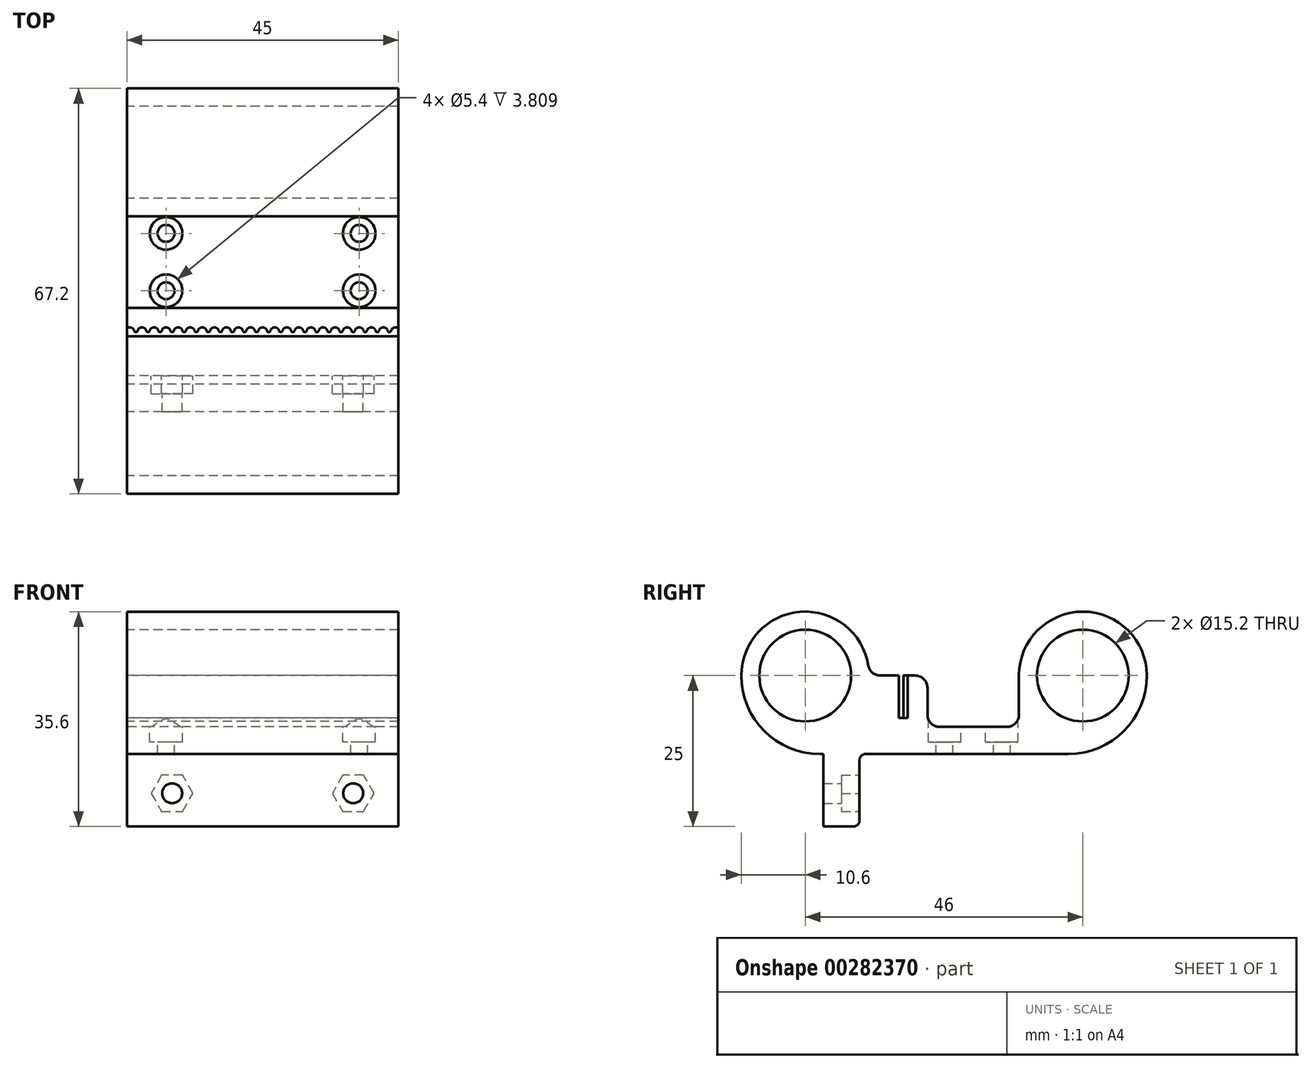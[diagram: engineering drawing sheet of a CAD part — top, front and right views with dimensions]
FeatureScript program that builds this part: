
annotation { "Feature Type Name" : "Feature", "Feature Type Description" : "" }
export const myFeature = defineFeature(function(context is Context, id is Id, definition is map)
    precondition{}
    {
        {
            var Q0;
            Q0=qCreatedBy(makeId("Right.planeOp"),FACE);
            var sketch = newSketch(context, id + "F0", { "sketchPlane" : qUnion([Q0])});
            skCircle(sketch, "E0", {"center": v(0, 0) * mm, "radius": 7.6 * mm});
            skLineSegment(sketch, "E1", {"start": v(0, 0) * mm, "end": v(46, 0) * mm, "construction": true});
            skCircle(sketch, "E2", {"center": v(46, 0) * mm, "radius": 7.6 * mm});
            skArc(sketch, "E3", {"start": v(10.47, 1.68) * mm, "mid": v(-0.84, 10.57) * mm, "end": v(-10.6, 0) * mm});
            skArc(sketch, "E4", {"start": v(56.6, 0) * mm, "mid": v(46, 10.6) * mm, "end": v(35.4, 0) * mm});
            skLineSegment(sketch, "E5", {"start": v(15.5, -7) * mm, "end": v(16.25, -7) * mm});
            skPoint(sketch, "E6.orphan", {"position": v(46, -7.6) * mm});
            skPoint(sketch, "E7.orphan", {"position": v(0, -7.6) * mm});
            skLineSegment(sketch, "E8", {"start": v(12.44, 0) * mm, "end": v(15.5, 0) * mm});
            skLineSegment(sketch, "E9", {"start": v(15.5, 0) * mm, "end": v(15.5, -7) * mm});
            skLineSegment(sketch, "E10", {"start": v(16.25, -7) * mm, "end": v(16.25, 0) * mm});
            skLineSegment(sketch, "E11", {"start": v(16.25, 0) * mm, "end": v(18.25, 0) * mm});
            skLineSegment(sketch, "E12", {"start": v(20.25, -2) * mm, "end": v(20.25, -6.5) * mm});
            skLineSegment(sketch, "E13.trimOffspring", {"start": v(22.25, -8.5) * mm, "end": v(33.4, -8.5) * mm});
            skLineSegment(sketch, "E14", {"start": v(35.4, 0) * mm, "end": v(35.4, -6.5) * mm});
            skPoint(sketch, "E15.visualSharp", {"position": v(20.25, 0) * mm});
            skArc(sketch, "E15.filletArc", {"start": v(20.25, -2) * mm, "mid": v(19.66, -0.59) * mm, "end": v(18.25, 0) * mm});
            skPoint(sketch, "E16.visualSharp", {"position": v(20.25, -8.5) * mm});
            skArc(sketch, "E16.filletArc", {"start": v(20.25, -6.5) * mm, "mid": v(20.84, -7.91) * mm, "end": v(22.25, -8.5) * mm});
            skPoint(sketch, "E17.visualSharp", {"position": v(35.4, -8.5) * mm});
            skArc(sketch, "E17.filletArc", {"start": v(33.4, -8.5) * mm, "mid": v(34.81, -7.91) * mm, "end": v(35.4, -6.5) * mm});
            skLineSegment(sketch, "E18", {"start": v(3, -25) * mm, "end": v(8, -25) * mm});
            skLineSegment(sketch, "E19", {"start": v(9, -24) * mm, "end": v(9, -14) * mm});
            skPoint(sketch, "E20.visualSharp", {"position": v(9, -13) * mm});
            skArc(sketch, "E20.filletArc", {"start": v(10, -13) * mm, "mid": v(9.3, -13.3) * mm, "end": v(9, -14) * mm});
            skPoint(sketch, "E21.visualSharp", {"position": v(9, -25) * mm});
            skArc(sketch, "E21.filletArc", {"start": v(8, -25) * mm, "mid": v(8.7, -24.7) * mm, "end": v(9, -24) * mm});
            skLineSegment(sketch, "E22", {"start": v(53.6, 0) * mm, "end": v(56.6, 0) * mm, "construction": true});
            skArc(sketch, "E23", {"start": v(43.6, -13) * mm, "mid": v(52.8, -9.2) * mm, "end": v(56.6, 0) * mm});
            skPoint(sketch, "E24.visualSharp", {"position": v(10.6, 0) * mm});
            skArc(sketch, "E24.filletArc", {"start": v(10.47, 1.68) * mm, "mid": v(11.14, 0.48) * mm, "end": v(12.44, 0) * mm});
            skLineSegment(sketch, "E25", {"start": v(9, -13) * mm, "end": v(3, -13) * mm, "construction": true});
            skLineSegment(sketch, "E26", {"start": v(10, -13) * mm, "end": v(43.6, -13) * mm});
            skLineSegment(sketch, "E27", {"start": v(3, -13) * mm, "end": v(3, -25) * mm});
            skLineSegment(sketch, "E28", {"start": v(2.4, -13) * mm, "end": v(3, -13) * mm});
            skLineSegment(sketch, "E29", {"start": v(23, 0) * mm, "end": v(23, 8.24) * mm, "construction": true});
            skArc(sketch, "E30.MirrorCS", {"start": v(2.4, -13) * mm, "mid": v(-6.8, -9.2) * mm, "end": v(-10.6, 0) * mm});
            skSolve(sketch);
        }
        {
            var Q0;
            Q0 = qSketchRegion(id + "F0", true);
            extrude(context, id + "F1", {"entities" : qUnion([Q0]), "depth" : 45 * mm});
        }
        {
            var Q0;
            Q0=makeQuery(id+"F1.opExtrude","SWEPT_FACE",FACE,{"disambiguationData":[OSD([sQuery(id+"F0.wireOp",EDGE,"E19")])]});
            var sketch = newSketch(context, id + "F2", { "sketchPlane" : qUnion([Q0])});
            skLineSegment(sketch, "E31", {"start": v(-45, -19.5) * mm, "end": v(0, -19.5) * mm, "construction": true});
            skLineSegment(sketch, "E32", {"start": v(-22.5, -19.5) * mm, "end": v(-22.5, -24) * mm, "construction": true});
            skCircle(sketch, "E33.cCircle", {"center": v(-37.5, -19.5) * mm, "radius": 3 * mm, "construction": true});
            skLineSegment(sketch, "E33.0", {"start": v(-35.77, -22.5) * mm, "end": v(-39.23, -22.5) * mm});
            skLineSegment(sketch, "E33.1", {"start": v(-39.23, -22.5) * mm, "end": v(-40.96, -19.5) * mm});
            skLineSegment(sketch, "E33.2", {"start": v(-40.96, -19.5) * mm, "end": v(-39.23, -16.5) * mm});
            skLineSegment(sketch, "E33.3", {"start": v(-39.23, -16.5) * mm, "end": v(-35.77, -16.5) * mm});
            skLineSegment(sketch, "E33.4", {"start": v(-35.77, -16.5) * mm, "end": v(-34.04, -19.5) * mm});
            skLineSegment(sketch, "E33.5", {"start": v(-34.04, -19.5) * mm, "end": v(-35.77, -22.5) * mm});
            skPoint(sketch, "E33.0.midPoint", {"position": v(-37.5, -22.5) * mm});
            skCircle(sketch, "E34.cCircle", {"center": v(-7.5, -19.5) * mm, "radius": 3 * mm, "construction": true});
            skLineSegment(sketch, "E34.0", {"start": v(-5.77, -22.5) * mm, "end": v(-9.23, -22.5) * mm});
            skLineSegment(sketch, "E34.1", {"start": v(-9.23, -22.5) * mm, "end": v(-10.96, -19.5) * mm});
            skLineSegment(sketch, "E34.2", {"start": v(-10.96, -19.5) * mm, "end": v(-9.23, -16.5) * mm});
            skLineSegment(sketch, "E34.3", {"start": v(-9.23, -16.5) * mm, "end": v(-5.77, -16.5) * mm});
            skLineSegment(sketch, "E34.4", {"start": v(-5.77, -16.5) * mm, "end": v(-4.04, -19.5) * mm});
            skLineSegment(sketch, "E34.5", {"start": v(-4.04, -19.5) * mm, "end": v(-5.77, -22.5) * mm});
            skPoint(sketch, "E34.0.midPoint", {"position": v(-7.5, -22.5) * mm});
            skSolve(sketch);
        }
        {
            var Q0;
            Q0 = qSketchRegion(id + "F2", true);
            extrude(context, id + "F3", {"entities" : qUnion([Q0]), "operationType" : NewBodyOperationType.REMOVE, "oppositeDirection" : true, "depth" : 3 * mm});
        }
        {
            var Q0;
            Q0=sQuery(id+"F2.wireOp",VERTEX,"E33.cCircle.center");
            var Q1;
            Q1=sQuery(id+"F2.wireOp",VERTEX,"E34.cCircle.center");
            var Q2;
            Q2=makeQuery(id+"F1.opExtrude","SWEPT_BODY",BODY,{"disambiguationData":[OSD([sQuery(id+"F0.wireOp",EDGE,"E0"),sQuery(id+"F0.wireOp",EDGE,"E2"),sQuery(id+"F0.wireOp",EDGE,"E3"),sQuery(id+"F0.wireOp",EDGE,"E4"),sQuery(id+"F0.wireOp",EDGE,"j08GQjmV-9Uym-nQLd-N5JK-njCeGAc3z8Nu"),sQuery(id+"F0.wireOp",EDGE,"E5"),sQuery(id+"F0.wireOp",EDGE,"E8"),sQuery(id+"F0.wireOp",EDGE,"E9"),sQuery(id+"F0.wireOp",EDGE,"E10"),sQuery(id+"F0.wireOp",EDGE,"E11"),sQuery(id+"F0.wireOp",EDGE,"E12"),sQuery(id+"F0.wireOp",EDGE,"E13.trimOffspring"),sQuery(id+"F0.wireOp",EDGE,"E14"),sQuery(id+"F0.wireOp",EDGE,"E15.filletArc"),sQuery(id+"F0.wireOp",EDGE,"E16.filletArc"),sQuery(id+"F0.wireOp",EDGE,"E17.filletArc"),sQuery(id+"F0.wireOp",EDGE,"HgORvXto-rNN1-qf5N-DkuC-96ioj9euDlec"),sQuery(id+"F0.wireOp",EDGE,"E18"),sQuery(id+"F0.wireOp",EDGE,"E19"),sQuery(id+"F0.wireOp",EDGE,"e149524c-0aa9-48c4-a7ad-8e2e2100d5f0.filletArc"),sQuery(id+"F0.wireOp",EDGE,"65fca797-e460-4261-b8cc-2deb6b025714.filletArc")])]});
            hole(context, id + "F4", {"style" : HoleStyle.SIMPLE, "endStyle" : HoleEndStyle.THROUGH, "standardTappedOrClearance" : lookupTablePath({ "standard" : "ISO", "fit" : "Normal", "size" : "M3", "type" : "Clearance" }), "standardBlindInLast" : lookupTablePath({ "fit" : "Standard", "standard" : "ISO", "size" : "M3", "type" : "Clearance" }), "holeDiameter" : 3.3 * mm, "tappedDepth" : 3 * mm, "tapClearance" : 3, "startFromSketch" : true, "locations" : qUnion([Q0, Q1]), "scope" : qUnion([Q2])});
        }
        {
            var Q0;
            Q0=makeQuery(id+"F1.opExtrude","SWEPT_FACE",FACE,{"disambiguationData":[OSD([sQuery(id+"F0.wireOp",EDGE,"E13.trimOffspring")])]});
            var sketch = newSketch(context, id + "F5", { "sketchPlane" : qUnion([Q0])});
            skLineSegment(sketch, "E35", {"start": v(0, 27.82) * mm, "end": v(45, 27.82) * mm, "construction": true});
            skLineSegment(sketch, "E36", {"start": v(6.5, 32.57) * mm, "end": v(6.5, 23.07) * mm, "construction": true});
            skLineSegment(sketch, "E37", {"start": v(38.5, 32.58) * mm, "end": v(38.5, 23.07) * mm, "construction": true});
            skCircle(sketch, "E38", {"center": v(6.5, 32.57) * mm, "radius": 1.4 * mm});
            skCircle(sketch, "E39", {"center": v(6.5, 23.07) * mm, "radius": 1.4 * mm});
            skCircle(sketch, "E40", {"center": v(38.5, 23.07) * mm, "radius": 1.4 * mm});
            skCircle(sketch, "E41", {"center": v(38.5, 32.58) * mm, "radius": 1.4 * mm});
            skSolve(sketch);
        }
        {
            var Q0;
            Q0 = qSketchRegion(id + "F5", true);
            extrude(context, id + "F6", {"entities" : qUnion([Q0]), "operationType" : NewBodyOperationType.REMOVE, "endBound" : BoundingType.SYMMETRIC, "oppositeDirection" : true, "depth" : 25 * mm});
        }
        {
            var Q0;
            Q0=makeQuery(id+"F1.opExtrude","SWEPT_FACE",FACE,{"disambiguationData":[OSD([sQuery(id+"F0.wireOp",EDGE,"E13.trimOffspring")])]});
            var sketch = newSketch(context, id + "F7", { "sketchPlane" : qUnion([Q0])});
            skCircle(sketch, "E42", {"center": v(6.5, 32.57) * mm, "radius": 2.7 * mm});
            skCircle(sketch, "E43", {"center": v(38.5, 32.58) * mm, "radius": 2.7 * mm});
            skCircle(sketch, "E44", {"center": v(38.5, 23.07) * mm, "radius": 2.7 * mm});
            skCircle(sketch, "E45", {"center": v(6.5, 23.07) * mm, "radius": 2.7 * mm});
            skSolve(sketch);
        }
        {
            var Q0;
            Q0 = qSketchRegion(id + "F7", true);
            extrude(context, id + "F8", {"entities" : qUnion([Q0]), "operationType" : NewBodyOperationType.REMOVE, "oppositeDirection" : true, "depth" : 2.5 * mm});
        }
        {
            var Q0;
            Q0=makeQuery(id+"F1.opExtrude","SWEPT_FACE",FACE,{"disambiguationData":[OSD([sQuery(id+"F0.wireOp",EDGE,"E13.trimOffspring")])]});
            var sketch = newSketch(context, id + "F9", { "sketchPlane" : qUnion([Q0])});
            skCircle(sketch, "E46", {"center": v(6.5, 32.57) * mm, "radius": 2.7 * mm});
            skCircle(sketch, "E47", {"center": v(38.5, 32.58) * mm, "radius": 2.7 * mm});
            skCircle(sketch, "E48", {"center": v(38.5, 23.07) * mm, "radius": 2.7 * mm});
            skCircle(sketch, "E49", {"center": v(6.5, 23.07) * mm, "radius": 2.7 * mm});
            skSolve(sketch);
        }
        {
            var Q0;
            Q0 = qSketchRegion(id + "F9", true);
            extrude(context, id + "F10", {"entities" : qUnion([Q0]), "operationType" : NewBodyOperationType.REMOVE, "depth" : 25 * mm});
        }
        {
            var Q0;
            Q0=makeQuery(id+"F1.opExtrude","SWEPT_FACE",FACE,{"disambiguationData":[OSD([sQuery(id+"F0.wireOp",EDGE,"E11")])]});
            var sketch = newSketch(context, id + "F11", { "sketchPlane" : qUnion([Q0])});
            skLineSegment(sketch, "E50", {"start": v(45, 17) * mm, "end": v(0, 17) * mm, "construction": true});
            skPoint(sketch, "E50.endSnap0", {"position": v(0, 17.25) * mm});
            skLineSegment(sketch, "E51", {"start": v(22.5, 17) * mm, "end": v(22.5, 16.25) * mm, "construction": true});
            skLineSegment(sketch, "E52", {"start": v(20.5, 17) * mm, "end": v(20.5, 16.25) * mm, "construction": true});
            skLineSegment(sketch, "E53", {"start": v(24.5, 17) * mm, "end": v(24.5, 16.25) * mm, "construction": true});
            skArc(sketch, "E54", {"start": v(23.24, 16.38) * mm, "mid": v(22.5, 17) * mm, "end": v(21.76, 16.38) * mm});
            skLineSegment(sketch, "E55", {"start": v(21.5, 16.25) * mm, "end": v(21.61, 16.25) * mm});
            skLineSegment(sketch, "E56", {"start": v(21.5, 17) * mm, "end": v(21.5, 16.25) * mm, "construction": true});
            skLineSegment(sketch, "E57", {"start": v(23.5, 17) * mm, "end": v(23.5, 16.25) * mm, "construction": true});
            skLineSegment(sketch, "E58", {"start": v(23.39, 16.25) * mm, "end": v(23.5, 16.25) * mm});
            skLineSegment(sketch, "E59", {"start": v(21.5, 16.25) * mm, "end": v(21.5, 16.05) * mm});
            skLineSegment(sketch, "E60", {"start": v(21.5, 16.05) * mm, "end": v(23.5, 16.05) * mm});
            skLineSegment(sketch, "E61", {"start": v(23.5, 16.05) * mm, "end": v(23.5, 16.25) * mm});
            skPoint(sketch, "E62.visualSharp", {"position": v(21.75, 16.25) * mm});
            skArc(sketch, "E62.filletArc", {"start": v(21.61, 16.25) * mm, "mid": v(21.7, 16.29) * mm, "end": v(21.76, 16.38) * mm});
            skPoint(sketch, "E63.visualSharp", {"position": v(23.25, 16.25) * mm});
            skArc(sketch, "E63.filletArc", {"start": v(23.24, 16.38) * mm, "mid": v(23.3, 16.29) * mm, "end": v(23.39, 16.25) * mm});
            skArc(sketch, "E64.1.0.0", {"start": v(25.24, 16.38) * mm, "mid": v(24.5, 17) * mm, "end": v(23.76, 16.38) * mm});
            skArc(sketch, "E64.1.0.1", {"start": v(23.61, 16.25) * mm, "mid": v(23.7, 16.29) * mm, "end": v(23.76, 16.38) * mm});
            skLineSegment(sketch, "E64.1.0.2", {"start": v(23.5, 16.25) * mm, "end": v(23.61, 16.25) * mm});
            skLineSegment(sketch, "E64.1.0.3", {"start": v(23.5, 16.25) * mm, "end": v(23.5, 16.05) * mm});
            skLineSegment(sketch, "E64.1.0.4", {"start": v(23.5, 16.05) * mm, "end": v(25.5, 16.05) * mm});
            skLineSegment(sketch, "E64.1.0.5", {"start": v(25.5, 16.05) * mm, "end": v(25.5, 16.25) * mm});
            skArc(sketch, "E64.1.0.6", {"start": v(25.24, 16.38) * mm, "mid": v(25.3, 16.29) * mm, "end": v(25.39, 16.25) * mm});
            skLineSegment(sketch, "E64.1.0.7", {"start": v(25.39, 16.25) * mm, "end": v(25.5, 16.25) * mm});
            skArc(sketch, "E64.2.0.0", {"start": v(27.24, 16.38) * mm, "mid": v(26.5, 17) * mm, "end": v(25.76, 16.38) * mm});
            skArc(sketch, "E64.2.0.1", {"start": v(25.61, 16.25) * mm, "mid": v(25.7, 16.29) * mm, "end": v(25.76, 16.38) * mm});
            skLineSegment(sketch, "E64.2.0.2", {"start": v(25.5, 16.25) * mm, "end": v(25.61, 16.25) * mm});
            skLineSegment(sketch, "E64.2.0.3", {"start": v(25.5, 16.25) * mm, "end": v(25.5, 16.05) * mm});
            skLineSegment(sketch, "E64.2.0.4", {"start": v(25.5, 16.05) * mm, "end": v(27.5, 16.05) * mm});
            skLineSegment(sketch, "E64.2.0.5", {"start": v(27.5, 16.05) * mm, "end": v(27.5, 16.25) * mm});
            skArc(sketch, "E64.2.0.6", {"start": v(27.24, 16.38) * mm, "mid": v(27.3, 16.29) * mm, "end": v(27.39, 16.25) * mm});
            skLineSegment(sketch, "E64.2.0.7", {"start": v(27.39, 16.25) * mm, "end": v(27.5, 16.25) * mm});
            skArc(sketch, "E64.3.0.0", {"start": v(29.24, 16.38) * mm, "mid": v(28.5, 17) * mm, "end": v(27.76, 16.38) * mm});
            skArc(sketch, "E64.3.0.1", {"start": v(27.61, 16.25) * mm, "mid": v(27.7, 16.29) * mm, "end": v(27.76, 16.38) * mm});
            skLineSegment(sketch, "E64.3.0.2", {"start": v(27.5, 16.25) * mm, "end": v(27.61, 16.25) * mm});
            skLineSegment(sketch, "E64.3.0.3", {"start": v(27.5, 16.25) * mm, "end": v(27.5, 16.05) * mm});
            skLineSegment(sketch, "E64.3.0.4", {"start": v(27.5, 16.05) * mm, "end": v(29.5, 16.05) * mm});
            skLineSegment(sketch, "E64.3.0.5", {"start": v(29.5, 16.05) * mm, "end": v(29.5, 16.25) * mm});
            skArc(sketch, "E64.3.0.6", {"start": v(29.24, 16.38) * mm, "mid": v(29.3, 16.29) * mm, "end": v(29.39, 16.25) * mm});
            skLineSegment(sketch, "E64.3.0.7", {"start": v(29.39, 16.25) * mm, "end": v(29.5, 16.25) * mm});
            skArc(sketch, "E64.4.0.0", {"start": v(31.24, 16.38) * mm, "mid": v(30.5, 17) * mm, "end": v(29.76, 16.38) * mm});
            skArc(sketch, "E64.4.0.1", {"start": v(29.61, 16.25) * mm, "mid": v(29.7, 16.29) * mm, "end": v(29.76, 16.38) * mm});
            skLineSegment(sketch, "E64.4.0.2", {"start": v(29.5, 16.25) * mm, "end": v(29.61, 16.25) * mm});
            skLineSegment(sketch, "E64.4.0.3", {"start": v(29.5, 16.25) * mm, "end": v(29.5, 16.05) * mm});
            skLineSegment(sketch, "E64.4.0.4", {"start": v(29.5, 16.05) * mm, "end": v(31.5, 16.05) * mm});
            skLineSegment(sketch, "E64.4.0.5", {"start": v(31.5, 16.05) * mm, "end": v(31.5, 16.25) * mm});
            skArc(sketch, "E64.4.0.6", {"start": v(31.24, 16.38) * mm, "mid": v(31.3, 16.29) * mm, "end": v(31.39, 16.25) * mm});
            skLineSegment(sketch, "E64.4.0.7", {"start": v(31.39, 16.25) * mm, "end": v(31.5, 16.25) * mm});
            skArc(sketch, "E64.5.0.0", {"start": v(33.24, 16.38) * mm, "mid": v(32.5, 17) * mm, "end": v(31.76, 16.38) * mm});
            skArc(sketch, "E64.5.0.1", {"start": v(31.61, 16.25) * mm, "mid": v(31.7, 16.29) * mm, "end": v(31.76, 16.38) * mm});
            skLineSegment(sketch, "E64.5.0.2", {"start": v(31.5, 16.25) * mm, "end": v(31.61, 16.25) * mm});
            skLineSegment(sketch, "E64.5.0.3", {"start": v(31.5, 16.25) * mm, "end": v(31.5, 16.05) * mm});
            skLineSegment(sketch, "E64.5.0.4", {"start": v(31.5, 16.05) * mm, "end": v(33.5, 16.05) * mm});
            skLineSegment(sketch, "E64.5.0.5", {"start": v(33.5, 16.05) * mm, "end": v(33.5, 16.25) * mm});
            skArc(sketch, "E64.5.0.6", {"start": v(33.24, 16.38) * mm, "mid": v(33.3, 16.29) * mm, "end": v(33.39, 16.25) * mm});
            skLineSegment(sketch, "E64.5.0.7", {"start": v(33.39, 16.25) * mm, "end": v(33.5, 16.25) * mm});
            skArc(sketch, "E64.6.0.0", {"start": v(35.24, 16.38) * mm, "mid": v(34.5, 17) * mm, "end": v(33.76, 16.38) * mm});
            skArc(sketch, "E64.6.0.1", {"start": v(33.61, 16.25) * mm, "mid": v(33.7, 16.29) * mm, "end": v(33.76, 16.38) * mm});
            skLineSegment(sketch, "E64.6.0.2", {"start": v(33.5, 16.25) * mm, "end": v(33.61, 16.25) * mm});
            skLineSegment(sketch, "E64.6.0.3", {"start": v(33.5, 16.25) * mm, "end": v(33.5, 16.05) * mm});
            skLineSegment(sketch, "E64.6.0.4", {"start": v(33.5, 16.05) * mm, "end": v(35.5, 16.05) * mm});
            skLineSegment(sketch, "E64.6.0.5", {"start": v(35.5, 16.05) * mm, "end": v(35.5, 16.25) * mm});
            skArc(sketch, "E64.6.0.6", {"start": v(35.24, 16.38) * mm, "mid": v(35.3, 16.29) * mm, "end": v(35.39, 16.25) * mm});
            skLineSegment(sketch, "E64.6.0.7", {"start": v(35.39, 16.25) * mm, "end": v(35.5, 16.25) * mm});
            skArc(sketch, "E64.7.0.0", {"start": v(37.24, 16.38) * mm, "mid": v(36.5, 17) * mm, "end": v(35.76, 16.38) * mm});
            skArc(sketch, "E64.7.0.1", {"start": v(35.61, 16.25) * mm, "mid": v(35.7, 16.29) * mm, "end": v(35.76, 16.38) * mm});
            skLineSegment(sketch, "E64.7.0.2", {"start": v(35.5, 16.25) * mm, "end": v(35.61, 16.25) * mm});
            skLineSegment(sketch, "E64.7.0.3", {"start": v(35.5, 16.25) * mm, "end": v(35.5, 16.05) * mm});
            skLineSegment(sketch, "E64.7.0.4", {"start": v(35.5, 16.05) * mm, "end": v(37.5, 16.05) * mm});
            skLineSegment(sketch, "E64.7.0.5", {"start": v(37.5, 16.05) * mm, "end": v(37.5, 16.25) * mm});
            skArc(sketch, "E64.7.0.6", {"start": v(37.24, 16.38) * mm, "mid": v(37.3, 16.29) * mm, "end": v(37.39, 16.25) * mm});
            skLineSegment(sketch, "E64.7.0.7", {"start": v(37.39, 16.25) * mm, "end": v(37.5, 16.25) * mm});
            skArc(sketch, "E64.8.0.0", {"start": v(39.24, 16.38) * mm, "mid": v(38.5, 17) * mm, "end": v(37.76, 16.38) * mm});
            skArc(sketch, "E64.8.0.1", {"start": v(37.61, 16.25) * mm, "mid": v(37.7, 16.29) * mm, "end": v(37.76, 16.38) * mm});
            skLineSegment(sketch, "E64.8.0.2", {"start": v(37.5, 16.25) * mm, "end": v(37.61, 16.25) * mm});
            skLineSegment(sketch, "E64.8.0.3", {"start": v(37.5, 16.25) * mm, "end": v(37.5, 16.05) * mm});
            skLineSegment(sketch, "E64.8.0.4", {"start": v(37.5, 16.05) * mm, "end": v(39.5, 16.05) * mm});
            skLineSegment(sketch, "E64.8.0.5", {"start": v(39.5, 16.05) * mm, "end": v(39.5, 16.25) * mm});
            skArc(sketch, "E64.8.0.6", {"start": v(39.24, 16.38) * mm, "mid": v(39.3, 16.29) * mm, "end": v(39.39, 16.25) * mm});
            skLineSegment(sketch, "E64.8.0.7", {"start": v(39.39, 16.25) * mm, "end": v(39.5, 16.25) * mm});
            skArc(sketch, "E64.9.0.0", {"start": v(41.24, 16.38) * mm, "mid": v(40.5, 17) * mm, "end": v(39.76, 16.38) * mm});
            skArc(sketch, "E64.9.0.1", {"start": v(39.61, 16.25) * mm, "mid": v(39.7, 16.29) * mm, "end": v(39.76, 16.38) * mm});
            skLineSegment(sketch, "E64.9.0.2", {"start": v(39.5, 16.25) * mm, "end": v(39.61, 16.25) * mm});
            skLineSegment(sketch, "E64.9.0.3", {"start": v(39.5, 16.25) * mm, "end": v(39.5, 16.05) * mm});
            skLineSegment(sketch, "E64.9.0.4", {"start": v(39.5, 16.05) * mm, "end": v(41.5, 16.05) * mm});
            skLineSegment(sketch, "E64.9.0.5", {"start": v(41.5, 16.05) * mm, "end": v(41.5, 16.25) * mm});
            skArc(sketch, "E64.9.0.6", {"start": v(41.24, 16.38) * mm, "mid": v(41.3, 16.29) * mm, "end": v(41.39, 16.25) * mm});
            skLineSegment(sketch, "E64.9.0.7", {"start": v(41.39, 16.25) * mm, "end": v(41.5, 16.25) * mm});
            skArc(sketch, "E64.10.0.0", {"start": v(43.24, 16.38) * mm, "mid": v(42.5, 17) * mm, "end": v(41.76, 16.38) * mm});
            skArc(sketch, "E64.10.0.1", {"start": v(41.61, 16.25) * mm, "mid": v(41.7, 16.29) * mm, "end": v(41.76, 16.38) * mm});
            skLineSegment(sketch, "E64.10.0.2", {"start": v(41.5, 16.25) * mm, "end": v(41.61, 16.25) * mm});
            skLineSegment(sketch, "E64.10.0.3", {"start": v(41.5, 16.25) * mm, "end": v(41.5, 16.05) * mm});
            skLineSegment(sketch, "E64.10.0.4", {"start": v(41.5, 16.05) * mm, "end": v(43.5, 16.05) * mm});
            skLineSegment(sketch, "E64.10.0.5", {"start": v(43.5, 16.05) * mm, "end": v(43.5, 16.25) * mm});
            skArc(sketch, "E64.10.0.6", {"start": v(43.24, 16.38) * mm, "mid": v(43.3, 16.29) * mm, "end": v(43.39, 16.25) * mm});
            skLineSegment(sketch, "E64.10.0.7", {"start": v(43.39, 16.25) * mm, "end": v(43.5, 16.25) * mm});
            skArc(sketch, "E64.11.0.0", {"start": v(44.5, 17) * mm, "mid": v(44.02, 16.82) * mm, "end": v(43.76, 16.38) * mm});
            skArc(sketch, "E64.11.0.1", {"start": v(43.61, 16.25) * mm, "mid": v(43.7, 16.29) * mm, "end": v(43.76, 16.38) * mm});
            skLineSegment(sketch, "E64.11.0.2", {"start": v(43.5, 16.25) * mm, "end": v(43.61, 16.25) * mm});
            skLineSegment(sketch, "E64.11.0.3", {"start": v(43.5, 16.25) * mm, "end": v(43.5, 16.05) * mm});
            skLineSegment(sketch, "E64.11.0.4", {"start": v(43.5, 16.05) * mm, "end": v(45.5, 16.05) * mm});
            skLineSegment(sketch, "E64.11.0.5", {"start": v(45.5, 16.05) * mm, "end": v(45.5, 17) * mm});
            skLineSegment(sketch, "E64.direction1", {"start": v(21.76, 16.38) * mm, "end": v(23.76, 16.38) * mm, "construction": true});
            skLineSegment(sketch, "E65.1.0.0", {"start": v(19.5, 16.05) * mm, "end": v(21.5, 16.05) * mm});
            skLineSegment(sketch, "E65.1.0.1", {"start": v(21.5, 16.05) * mm, "end": v(21.5, 16.25) * mm});
            skLineSegment(sketch, "E65.1.0.2", {"start": v(21.39, 16.25) * mm, "end": v(21.5, 16.25) * mm});
            skArc(sketch, "E65.1.0.3", {"start": v(21.24, 16.38) * mm, "mid": v(21.3, 16.29) * mm, "end": v(21.39, 16.25) * mm});
            skArc(sketch, "E65.1.0.4", {"start": v(21.24, 16.38) * mm, "mid": v(20.5, 17) * mm, "end": v(19.76, 16.38) * mm});
            skArc(sketch, "E65.1.0.5", {"start": v(19.61, 16.25) * mm, "mid": v(19.7, 16.29) * mm, "end": v(19.76, 16.38) * mm});
            skLineSegment(sketch, "E65.1.0.6", {"start": v(19.5, 16.25) * mm, "end": v(19.61, 16.25) * mm});
            skLineSegment(sketch, "E65.1.0.7", {"start": v(19.5, 16.25) * mm, "end": v(19.5, 16.05) * mm});
            skLineSegment(sketch, "E65.2.0.0", {"start": v(17.5, 16.05) * mm, "end": v(19.5, 16.05) * mm});
            skLineSegment(sketch, "E65.2.0.1", {"start": v(19.5, 16.05) * mm, "end": v(19.5, 16.25) * mm});
            skLineSegment(sketch, "E65.2.0.2", {"start": v(19.39, 16.25) * mm, "end": v(19.5, 16.25) * mm});
            skArc(sketch, "E65.2.0.3", {"start": v(19.24, 16.38) * mm, "mid": v(19.3, 16.29) * mm, "end": v(19.39, 16.25) * mm});
            skArc(sketch, "E65.2.0.4", {"start": v(19.24, 16.38) * mm, "mid": v(18.5, 17) * mm, "end": v(17.76, 16.38) * mm});
            skArc(sketch, "E65.2.0.5", {"start": v(17.61, 16.25) * mm, "mid": v(17.7, 16.29) * mm, "end": v(17.76, 16.38) * mm});
            skLineSegment(sketch, "E65.2.0.6", {"start": v(17.5, 16.25) * mm, "end": v(17.61, 16.25) * mm});
            skLineSegment(sketch, "E65.2.0.7", {"start": v(17.5, 16.25) * mm, "end": v(17.5, 16.05) * mm});
            skLineSegment(sketch, "E65.3.0.0", {"start": v(15.5, 16.05) * mm, "end": v(17.5, 16.05) * mm});
            skLineSegment(sketch, "E65.3.0.1", {"start": v(17.5, 16.05) * mm, "end": v(17.5, 16.25) * mm});
            skLineSegment(sketch, "E65.3.0.2", {"start": v(17.39, 16.25) * mm, "end": v(17.5, 16.25) * mm});
            skArc(sketch, "E65.3.0.3", {"start": v(17.24, 16.38) * mm, "mid": v(17.3, 16.29) * mm, "end": v(17.39, 16.25) * mm});
            skArc(sketch, "E65.3.0.4", {"start": v(17.24, 16.38) * mm, "mid": v(16.5, 17) * mm, "end": v(15.76, 16.38) * mm});
            skArc(sketch, "E65.3.0.5", {"start": v(15.61, 16.25) * mm, "mid": v(15.7, 16.29) * mm, "end": v(15.76, 16.38) * mm});
            skLineSegment(sketch, "E65.3.0.6", {"start": v(15.5, 16.25) * mm, "end": v(15.61, 16.25) * mm});
            skLineSegment(sketch, "E65.3.0.7", {"start": v(15.5, 16.25) * mm, "end": v(15.5, 16.05) * mm});
            skLineSegment(sketch, "E65.4.0.0", {"start": v(13.5, 16.05) * mm, "end": v(15.5, 16.05) * mm});
            skLineSegment(sketch, "E65.4.0.1", {"start": v(15.5, 16.05) * mm, "end": v(15.5, 16.25) * mm});
            skLineSegment(sketch, "E65.4.0.2", {"start": v(15.39, 16.25) * mm, "end": v(15.5, 16.25) * mm});
            skArc(sketch, "E65.4.0.3", {"start": v(15.24, 16.38) * mm, "mid": v(15.3, 16.29) * mm, "end": v(15.39, 16.25) * mm});
            skArc(sketch, "E65.4.0.4", {"start": v(15.24, 16.38) * mm, "mid": v(14.5, 17) * mm, "end": v(13.76, 16.38) * mm});
            skArc(sketch, "E65.4.0.5", {"start": v(13.61, 16.25) * mm, "mid": v(13.7, 16.29) * mm, "end": v(13.76, 16.38) * mm});
            skLineSegment(sketch, "E65.4.0.6", {"start": v(13.5, 16.25) * mm, "end": v(13.61, 16.25) * mm});
            skLineSegment(sketch, "E65.4.0.7", {"start": v(13.5, 16.25) * mm, "end": v(13.5, 16.05) * mm});
            skLineSegment(sketch, "E65.5.0.0", {"start": v(11.5, 16.05) * mm, "end": v(13.5, 16.05) * mm});
            skLineSegment(sketch, "E65.5.0.1", {"start": v(13.5, 16.05) * mm, "end": v(13.5, 16.25) * mm});
            skLineSegment(sketch, "E65.5.0.2", {"start": v(13.39, 16.25) * mm, "end": v(13.5, 16.25) * mm});
            skArc(sketch, "E65.5.0.3", {"start": v(13.24, 16.38) * mm, "mid": v(13.3, 16.29) * mm, "end": v(13.39, 16.25) * mm});
            skArc(sketch, "E65.5.0.4", {"start": v(13.24, 16.38) * mm, "mid": v(12.5, 17) * mm, "end": v(11.76, 16.38) * mm});
            skArc(sketch, "E65.5.0.5", {"start": v(11.61, 16.25) * mm, "mid": v(11.7, 16.29) * mm, "end": v(11.76, 16.38) * mm});
            skLineSegment(sketch, "E65.5.0.6", {"start": v(11.5, 16.25) * mm, "end": v(11.61, 16.25) * mm});
            skLineSegment(sketch, "E65.5.0.7", {"start": v(11.5, 16.25) * mm, "end": v(11.5, 16.05) * mm});
            skLineSegment(sketch, "E65.6.0.0", {"start": v(9.5, 16.05) * mm, "end": v(11.5, 16.05) * mm});
            skLineSegment(sketch, "E65.6.0.1", {"start": v(11.5, 16.05) * mm, "end": v(11.5, 16.25) * mm});
            skLineSegment(sketch, "E65.6.0.2", {"start": v(11.39, 16.25) * mm, "end": v(11.5, 16.25) * mm});
            skArc(sketch, "E65.6.0.3", {"start": v(11.24, 16.38) * mm, "mid": v(11.3, 16.29) * mm, "end": v(11.39, 16.25) * mm});
            skArc(sketch, "E65.6.0.4", {"start": v(11.24, 16.38) * mm, "mid": v(10.5, 17) * mm, "end": v(9.76, 16.38) * mm});
            skArc(sketch, "E65.6.0.5", {"start": v(9.61, 16.25) * mm, "mid": v(9.7, 16.29) * mm, "end": v(9.76, 16.38) * mm});
            skLineSegment(sketch, "E65.6.0.6", {"start": v(9.5, 16.25) * mm, "end": v(9.61, 16.25) * mm});
            skLineSegment(sketch, "E65.6.0.7", {"start": v(9.5, 16.25) * mm, "end": v(9.5, 16.05) * mm});
            skLineSegment(sketch, "E65.7.0.0", {"start": v(7.5, 16.05) * mm, "end": v(9.5, 16.05) * mm});
            skLineSegment(sketch, "E65.7.0.1", {"start": v(9.5, 16.05) * mm, "end": v(9.5, 16.25) * mm});
            skLineSegment(sketch, "E65.7.0.2", {"start": v(9.39, 16.25) * mm, "end": v(9.5, 16.25) * mm});
            skArc(sketch, "E65.7.0.3", {"start": v(9.24, 16.38) * mm, "mid": v(9.3, 16.29) * mm, "end": v(9.39, 16.25) * mm});
            skArc(sketch, "E65.7.0.4", {"start": v(9.24, 16.38) * mm, "mid": v(8.5, 17) * mm, "end": v(7.76, 16.38) * mm});
            skArc(sketch, "E65.7.0.5", {"start": v(7.61, 16.25) * mm, "mid": v(7.7, 16.29) * mm, "end": v(7.76, 16.38) * mm});
            skLineSegment(sketch, "E65.7.0.6", {"start": v(7.5, 16.25) * mm, "end": v(7.61, 16.25) * mm});
            skLineSegment(sketch, "E65.7.0.7", {"start": v(7.5, 16.25) * mm, "end": v(7.5, 16.05) * mm});
            skLineSegment(sketch, "E65.8.0.0", {"start": v(5.5, 16.05) * mm, "end": v(7.5, 16.05) * mm});
            skLineSegment(sketch, "E65.8.0.1", {"start": v(7.5, 16.05) * mm, "end": v(7.5, 16.25) * mm});
            skLineSegment(sketch, "E65.8.0.2", {"start": v(7.39, 16.25) * mm, "end": v(7.5, 16.25) * mm});
            skArc(sketch, "E65.8.0.3", {"start": v(7.24, 16.38) * mm, "mid": v(7.3, 16.29) * mm, "end": v(7.39, 16.25) * mm});
            skArc(sketch, "E65.8.0.4", {"start": v(7.24, 16.38) * mm, "mid": v(6.5, 17) * mm, "end": v(5.76, 16.38) * mm});
            skArc(sketch, "E65.8.0.5", {"start": v(5.61, 16.25) * mm, "mid": v(5.7, 16.29) * mm, "end": v(5.76, 16.38) * mm});
            skLineSegment(sketch, "E65.8.0.6", {"start": v(5.5, 16.25) * mm, "end": v(5.61, 16.25) * mm});
            skLineSegment(sketch, "E65.8.0.7", {"start": v(5.5, 16.25) * mm, "end": v(5.5, 16.05) * mm});
            skLineSegment(sketch, "E65.9.0.0", {"start": v(3.5, 16.05) * mm, "end": v(5.5, 16.05) * mm});
            skLineSegment(sketch, "E65.9.0.1", {"start": v(5.5, 16.05) * mm, "end": v(5.5, 16.25) * mm});
            skLineSegment(sketch, "E65.9.0.2", {"start": v(5.39, 16.25) * mm, "end": v(5.5, 16.25) * mm});
            skArc(sketch, "E65.9.0.3", {"start": v(5.24, 16.38) * mm, "mid": v(5.3, 16.29) * mm, "end": v(5.39, 16.25) * mm});
            skArc(sketch, "E65.9.0.4", {"start": v(5.24, 16.38) * mm, "mid": v(4.5, 17) * mm, "end": v(3.76, 16.38) * mm});
            skArc(sketch, "E65.9.0.5", {"start": v(3.61, 16.25) * mm, "mid": v(3.7, 16.29) * mm, "end": v(3.76, 16.38) * mm});
            skLineSegment(sketch, "E65.9.0.6", {"start": v(3.5, 16.25) * mm, "end": v(3.61, 16.25) * mm});
            skLineSegment(sketch, "E65.9.0.7", {"start": v(3.5, 16.25) * mm, "end": v(3.5, 16.05) * mm});
            skLineSegment(sketch, "E65.10.0.0", {"start": v(1.5, 16.05) * mm, "end": v(3.5, 16.05) * mm});
            skLineSegment(sketch, "E65.10.0.1", {"start": v(3.5, 16.05) * mm, "end": v(3.5, 16.25) * mm});
            skLineSegment(sketch, "E65.10.0.2", {"start": v(3.39, 16.25) * mm, "end": v(3.5, 16.25) * mm});
            skArc(sketch, "E65.10.0.3", {"start": v(3.24, 16.38) * mm, "mid": v(3.3, 16.29) * mm, "end": v(3.39, 16.25) * mm});
            skArc(sketch, "E65.10.0.4", {"start": v(3.24, 16.38) * mm, "mid": v(2.5, 17) * mm, "end": v(1.76, 16.38) * mm});
            skArc(sketch, "E65.10.0.5", {"start": v(1.61, 16.25) * mm, "mid": v(1.7, 16.29) * mm, "end": v(1.76, 16.38) * mm});
            skLineSegment(sketch, "E65.10.0.6", {"start": v(1.5, 16.25) * mm, "end": v(1.61, 16.25) * mm});
            skLineSegment(sketch, "E65.10.0.7", {"start": v(1.5, 16.25) * mm, "end": v(1.5, 16.05) * mm});
            skLineSegment(sketch, "E65.11.0.0", {"start": v(-0.5, 16.05) * mm, "end": v(1.5, 16.05) * mm});
            skLineSegment(sketch, "E65.11.0.1", {"start": v(1.5, 16.05) * mm, "end": v(1.5, 16.25) * mm});
            skLineSegment(sketch, "E65.11.0.2", {"start": v(1.39, 16.25) * mm, "end": v(1.5, 16.25) * mm});
            skArc(sketch, "E65.11.0.3", {"start": v(1.24, 16.38) * mm, "mid": v(1.3, 16.29) * mm, "end": v(1.39, 16.25) * mm});
            skArc(sketch, "E65.11.0.4", {"start": v(1.24, 16.38) * mm, "mid": v(0.98, 16.82) * mm, "end": v(0.5, 17) * mm});
            skLineSegment(sketch, "E65.11.0.7", {"start": v(-0.5, 17) * mm, "end": v(-0.5, 16.05) * mm});
            skLineSegment(sketch, "E65.direction1", {"start": v(21.5, 16.05) * mm, "end": v(19.5, 16.05) * mm, "construction": true});
            skLineSegment(sketch, "E66", {"start": v(44.5, 17) * mm, "end": v(45.5, 17) * mm});
            skLineSegment(sketch, "E67", {"start": v(0.5, 17) * mm, "end": v(-0.5, 17) * mm});
            skSolve(sketch);
        }
        {
            var Q0;
            Q0 = qSketchRegion(id + "F11", true);
            extrude(context, id + "F12", {"entities" : qUnion([Q0]), "operationType" : NewBodyOperationType.REMOVE, "oppositeDirection" : true, "depth" : 7 * mm});
        }
    });
